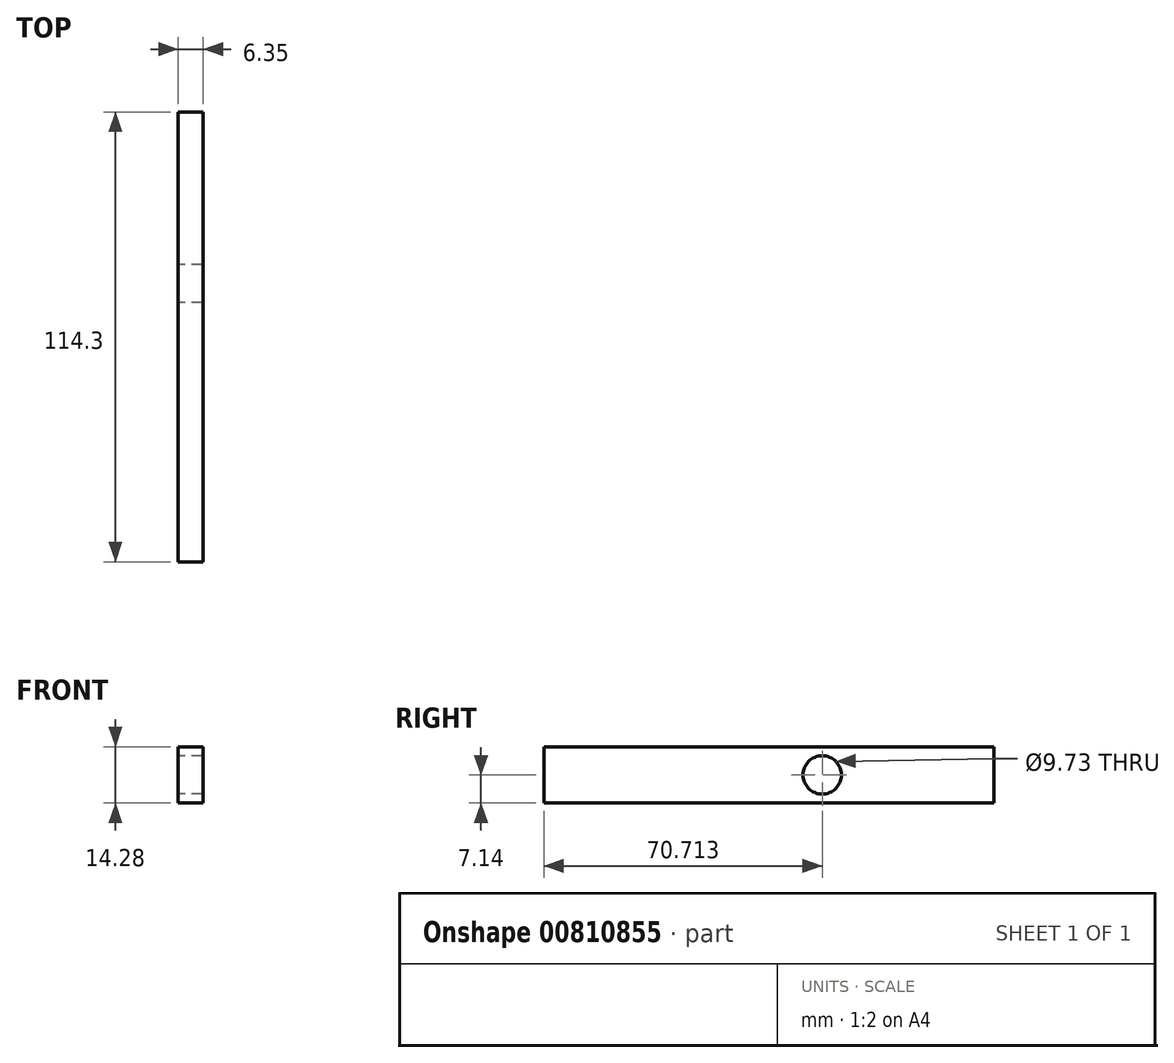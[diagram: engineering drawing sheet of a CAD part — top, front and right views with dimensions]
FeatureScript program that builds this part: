
annotation { "Feature Type Name" : "Feature", "Feature Type Description" : "" }
export const myFeature = defineFeature(function(context is Context, id is Id, definition is map)
    precondition{}
    {
        {
            var Q0;
            Q0=qCreatedBy(makeId("Right.planeOp"),FACE);
            var sketch = newSketch(context, id + "F0", { "sketchPlane" : qUnion([Q0])});
            skLineSegment(sketch, "E0.bottom", {"start": v(57.15, 7.14) * mm, "end": v(-57.15, 7.14) * mm});
            skLineSegment(sketch, "E0.top", {"start": v(57.15, -7.14) * mm, "end": v(-57.15, -7.14) * mm});
            skLineSegment(sketch, "E0.left", {"start": v(57.15, 7.14) * mm, "end": v(57.15, -7.14) * mm});
            skLineSegment(sketch, "E0.right", {"start": v(-57.15, 7.14) * mm, "end": v(-57.15, -7.14) * mm});
            skPoint(sketch, "E0.middle", {"position": v(0, 0) * mm});
            skCircle(sketch, "E1", {"center": v(13.56, 0) * mm, "radius": 4.87 * mm});
            skSolve(sketch);
        }
        {
            var Q0;
            Q0=makeQuery(id+"F0.imprint","IMPRINT",FACE,{"disambiguationData":[TD([[makeQuery(id+"F0.imprint","IMPRINT",EDGE,{"derivedFrom":sQuery(id+"F0.wireOp",EDGE,"E0.bottom")}),1.0]])]});
            extrude(context, id + "F1", {"entities" : qUnion([Q0]), "depth" : 6.35 * mm, "offsetDistance" : 25.4 * mm});
        }
    });
